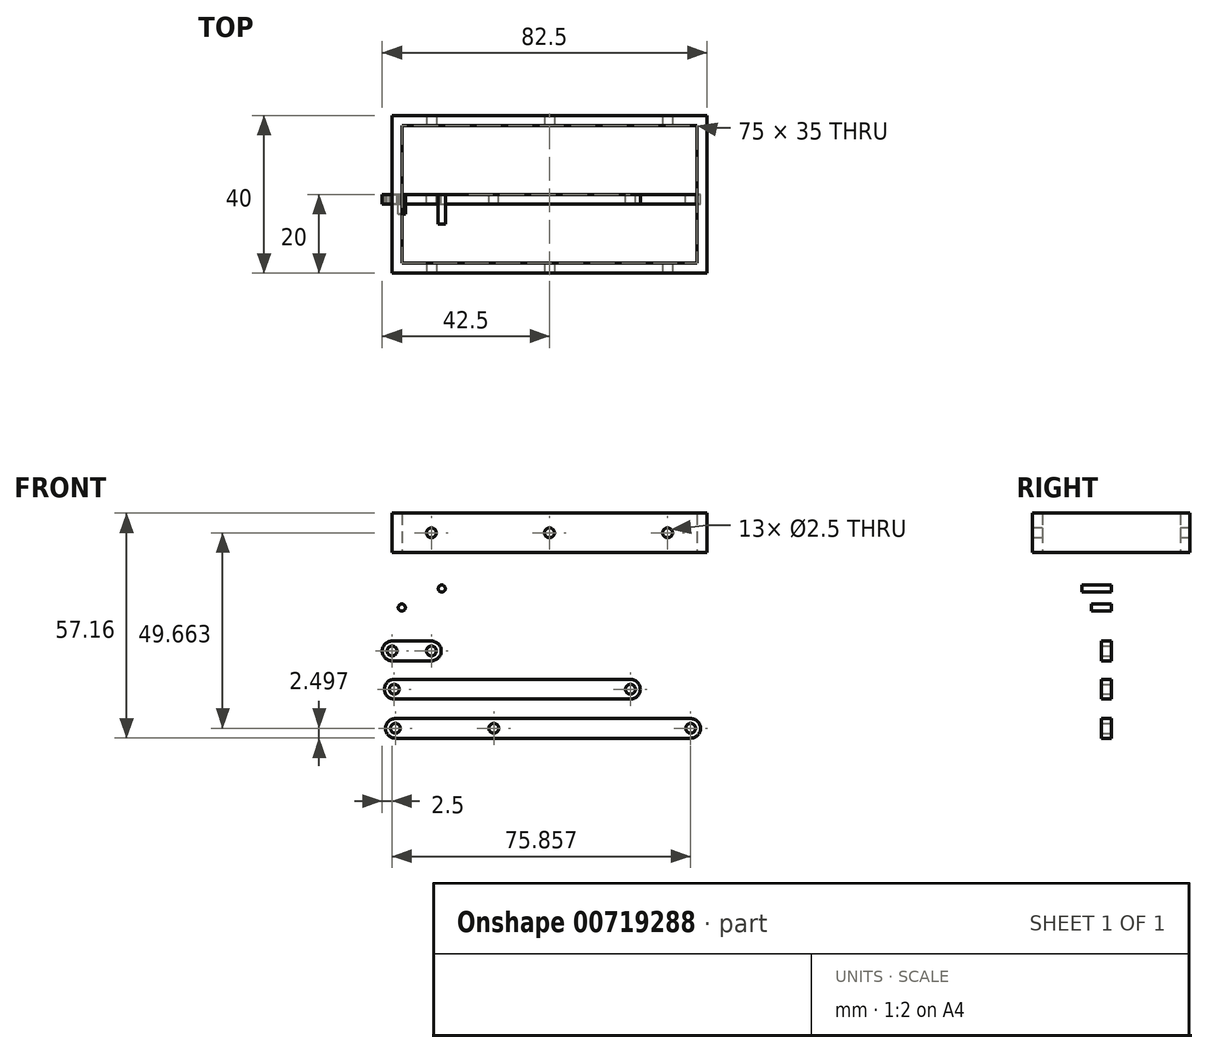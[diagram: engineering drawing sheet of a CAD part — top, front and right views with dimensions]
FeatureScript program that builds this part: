
annotation { "Feature Type Name" : "Feature", "Feature Type Description" : "" }
export const myFeature = defineFeature(function(context is Context, id is Id, definition is map)
    precondition{}
    {
        {
            assignVariable(context, id + "F0", {"name" : "thickness", "anyValue" : 2.5});
        }
        {
            var Q0;
            Q0=qCreatedBy(makeId("Front.planeOp"),FACE);
            var sketch = newSketch(context, id + "F1", { "sketchPlane" : qUnion([Q0])});
            skArc(sketch, "E0", {"start": v(0, 2.5) * mm, "mid": v(-2.5, 0) * mm, "end": v(0, -2.5) * mm});
            skArc(sketch, "E1", {"start": v(10, -2.5) * mm, "mid": v(12.5, 0) * mm, "end": v(10, 2.5) * mm});
            skLineSegment(sketch, "E2", {"start": v(0, 2.5) * mm, "end": v(10, 2.5) * mm});
            skLineSegment(sketch, "E3", {"start": v(0, -2.5) * mm, "end": v(10, -2.5) * mm});
            skCircle(sketch, "E4", {"center": v(0, 0) * mm, "radius": 1.25 * mm});
            skCircle(sketch, "E5", {"center": v(10, 0) * mm, "radius": 1.25 * mm});
            skSolve(sketch);
        }
        {
            var Q0;
            Q0=makeQuery(id+"F1.imprint","IMPRINT",FACE,{"disambiguationData":[TD([[makeQuery(id+"F1.imprint","IMPRINT",EDGE,{"derivedFrom":sQuery(id+"F1.wireOp",EDGE,"E0")}),1.0]])]});
            extrude(context, id + "F2", {"entities" : qUnion([Q0]), "depth" : (getVariable(context, 'thickness')) * mm, "offsetDistance" : 25 * mm});
        }
        {
            var Q0;
            Q0=qCreatedBy(makeId("Front.planeOp"),FACE);
            var sketch = newSketch(context, id + "F3", { "sketchPlane" : qUnion([Q0])});
            skArc(sketch, "E6", {"start": v(0.57, -7.23) * mm, "mid": v(-1.93, -9.73) * mm, "end": v(0.57, -12.23) * mm});
            skArc(sketch, "E7", {"start": v(60.57, -12.23) * mm, "mid": v(63.07, -9.73) * mm, "end": v(60.57, -7.23) * mm});
            skLineSegment(sketch, "E8", {"start": v(0.57, -7.23) * mm, "end": v(60.57, -7.23) * mm});
            skLineSegment(sketch, "E9", {"start": v(0.57, -12.23) * mm, "end": v(60.57, -12.23) * mm});
            skCircle(sketch, "E10", {"center": v(0.57, -9.73) * mm, "radius": 1.25 * mm});
            skCircle(sketch, "E11", {"center": v(60.57, -9.73) * mm, "radius": 1.25 * mm});
            skSolve(sketch);
        }
        {
            var Q0;
            Q0=makeQuery(id+"F3.imprint","IMPRINT",FACE,{"disambiguationData":[TD([[makeQuery(id+"F3.imprint","IMPRINT",EDGE,{"derivedFrom":sQuery(id+"F3.wireOp",EDGE,"E6")}),1.0]])]});
            extrude(context, id + "F4", {"entities" : qUnion([Q0]), "depth" : (getVariable(context, 'thickness')) * mm, "offsetDistance" : 25 * mm});
        }
        {
            var Q0;
            Q0=qCreatedBy(makeId("Front.planeOp"),FACE);
            var sketch = newSketch(context, id + "F5", { "sketchPlane" : qUnion([Q0])});
            skArc(sketch, "E12", {"start": v(0.86, -17.16) * mm, "mid": v(-1.64, -19.66) * mm, "end": v(0.86, -22.16) * mm});
            skArc(sketch, "E13", {"start": v(75.86, -22.16) * mm, "mid": v(78.36, -19.66) * mm, "end": v(75.86, -17.16) * mm});
            skLineSegment(sketch, "E14", {"start": v(0.86, -17.16) * mm, "end": v(75.86, -17.16) * mm});
            skLineSegment(sketch, "E15", {"start": v(0.86, -22.16) * mm, "end": v(75.86, -22.16) * mm});
            skCircle(sketch, "E16", {"center": v(0.86, -19.66) * mm, "radius": 1.25 * mm});
            skCircle(sketch, "E17", {"center": v(75.86, -19.66) * mm, "radius": 1.25 * mm});
            skCircle(sketch, "E18", {"center": v(25.86, -19.66) * mm, "radius": 1.25 * mm});
            skSolve(sketch);
        }
        {
            var Q0;
            Q0=makeQuery(id+"F5.imprint","IMPRINT",FACE,{"disambiguationData":[TD([[makeQuery(id+"F5.imprint","IMPRINT",EDGE,{"derivedFrom":sQuery(id+"F5.wireOp",EDGE,"E12")}),1.0]])]});
            extrude(context, id + "F6", {"entities" : qUnion([Q0]), "depth" : (getVariable(context, 'thickness')) * mm, "offsetDistance" : 25 * mm});
        }
        {
            var Q0;
            Q0=qCreatedBy(makeId("Top.planeOp"),FACE);
            cPlane(context, id + "F7", {"entities" : qUnion([Q0]), "cplaneType" : CPlaneType.OFFSET, "offset" : 25 * mm, "width" : 150 * mm, "height" : 150 * mm});
        }
        {
            var Q0;
            Q0=qCreatedBy(id+"F7.planeOp",FACE);
            var sketch = newSketch(context, id + "F8", { "sketchPlane" : qUnion([Q0])});
            skLineSegment(sketch, "E19.bottom", {"start": v(0, 20) * mm, "end": v(80, 20) * mm});
            skLineSegment(sketch, "E19.top", {"start": v(0, -20) * mm, "end": v(80, -20) * mm});
            skLineSegment(sketch, "E19.left", {"start": v(0, 20) * mm, "end": v(0, -20) * mm});
            skLineSegment(sketch, "E19.right", {"start": v(80, 20) * mm, "end": v(80, -20) * mm});
            skLineSegment(sketch, "E20.0", {"start": v(2.5, 17.5) * mm, "end": v(77.5, 17.5) * mm});
            skLineSegment(sketch, "E20.1", {"start": v(2.5, 17.5) * mm, "end": v(2.5, -17.5) * mm});
            skLineSegment(sketch, "E20.2", {"start": v(2.5, -17.5) * mm, "end": v(77.5, -17.5) * mm});
            skLineSegment(sketch, "E20.3", {"start": v(77.5, 17.5) * mm, "end": v(77.5, -17.5) * mm});
            skSolve(sketch);
        }
        {
            var Q0;
            Q0=makeQuery(id+"F8.imprint","IMPRINT",FACE,{"disambiguationData":[TD([[makeQuery(id+"F8.imprint","IMPRINT",EDGE,{"derivedFrom":sQuery(id+"F8.wireOp",EDGE,"E19.bottom")}),-1.0]])]});
            extrude(context, id + "F9", {"entities" : qUnion([Q0]), "depth" : 10 * mm, "offsetDistance" : 25 * mm});
        }
        {
            var Q0;
            Q0=makeQuery(id+"F9.opExtrude","SWEPT_FACE",FACE,{"disambiguationData":[OSD([sQuery(id+"F8.wireOp",EDGE,"E19.top")])]});
            var sketch = newSketch(context, id + "F10", { "sketchPlane" : qUnion([Q0])});
            skCircle(sketch, "E21", {"center": v(10, 30) * mm, "radius": 1.25 * mm});
            skCircle(sketch, "E22", {"center": v(70, 30) * mm, "radius": 1.25 * mm});
            skCircle(sketch, "E23", {"center": v(40, 30) * mm, "radius": 1.25 * mm});
            skPoint(sketch, "E23.centerSnap0", {"position": v(40, 25) * mm});
            skSolve(sketch);
        }
        {
            var Q0;
            Q0=qSketchRegion(id+"F10",true);
            extrude(context, id + "F11", {"entities" : qUnion([Q0]), "operationType" : NewBodyOperationType.REMOVE, "endBound" : BoundingType.THROUGH_ALL, "oppositeDirection" : true, "depth" : 25 * mm, "offsetDistance" : 25 * mm});
        }
        {
            var Q0;
            Q0=qCreatedBy(makeId("Front.planeOp"),FACE);
            var sketch = newSketch(context, id + "F12", { "sketchPlane" : qUnion([Q0])});
            skCircle(sketch, "E24", {"center": v(2.49, 11.02) * mm, "radius": 0.9 * mm});
            skSolve(sketch);
        }
        {
            var Q0;
            Q0=makeQuery(id+"F12.imprint","IMPRINT",FACE,{"disambiguationData":[TD([[makeQuery(id+"F12.imprint","IMPRINT",EDGE,{"derivedFrom":sQuery(id+"F12.wireOp",EDGE,"E24")}),1.0]])]});
            extrude(context, id + "F13", {"entities" : qUnion([Q0]), "depth" : (getVariable(context, 'thickness') * 2) * mm, "offsetDistance" : 25 * mm});
        }
        {
            var Q0;
            Q0=qCreatedBy(makeId("Front.planeOp"),FACE);
            var sketch = newSketch(context, id + "F14", { "sketchPlane" : qUnion([Q0])});
            skCircle(sketch, "E25", {"center": v(12.64, 15.84) * mm, "radius": 0.9 * mm});
            skSolve(sketch);
        }
        {
            var Q0;
            Q0 = qSketchRegion(id + "F14", true);
            extrude(context, id + "F15", {"entities" : qUnion([Q0]), "depth" : 7.5 * mm, "offsetDistance" : 25 * mm});
        }
    });
